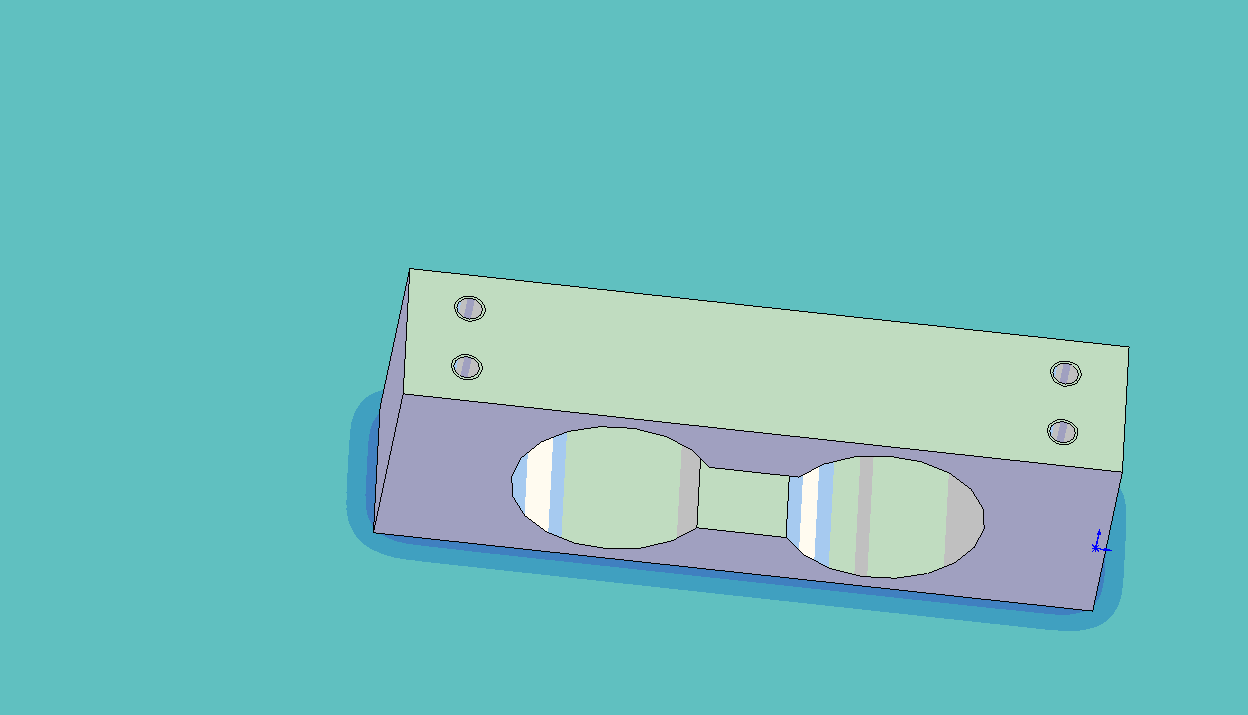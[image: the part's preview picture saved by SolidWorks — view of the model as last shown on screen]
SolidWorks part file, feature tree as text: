
SOLIDWORKS PART (.sldprt)
format: sldprt  version: not decoded by parser v0  size: 242,176 bytes
history: native  units: mm
features: thread x4, plane x3, sketch x3, material x1, extrude x1, hole x1 (+10 scaffold rows collapsed)
feature tree (23):
  scaffold x10  (default folders/planes/origin — collapsed)
  material  "Matériau <non spécifié>"
  plane  "Plan de face"
  plane  "Plan de dessus"
  plane  "Plan de droite"
  sketch  "Esquisse1"  dims[D4=20.0mm D1=70.0mm D2=23.0mm D3=26.0mm D5=5.0mm D6=5.0mm]
  extrude  "Extrusion1"  Depth=15mm
  hole  "Trou taraudé M3x0.51"  [1 undecoded]
  sketch  "Esquisse3D1"  dims[c1.D1=7.0mm c1.D2=~6.086849mm c1.D3=~7.001132mm c2.D3=~178.96952deg c2.D2=6.0mm c3.D3=6.0mm]
  thread  "Filetage de perçage1"  Diameter=3mm  [1 undecoded]
  thread  "Filetage de perçage2"  Diameter=3mm  [1 undecoded]
  thread  "Filetage de perçage3"  Diameter=3mm  [1 undecoded]
  thread  "Filetage de perçage4"  Diameter=3mm  [1 undecoded]
  sketch  "Esquisse2"  dims[hole-wizard template sketch: 60 standard entries collapsed; hole parameters kept: c18.Profondeur du trou pour taraudage jusqu'au prochain=23.0mm]
decode coverage: 8 of 9 modeling features carry decoded parameters
note: ~ marks probable driven/reference dimensions
note: 5 parameter values undecoded
note: suppression state not decoded; provenance and decode notes live in map.json
